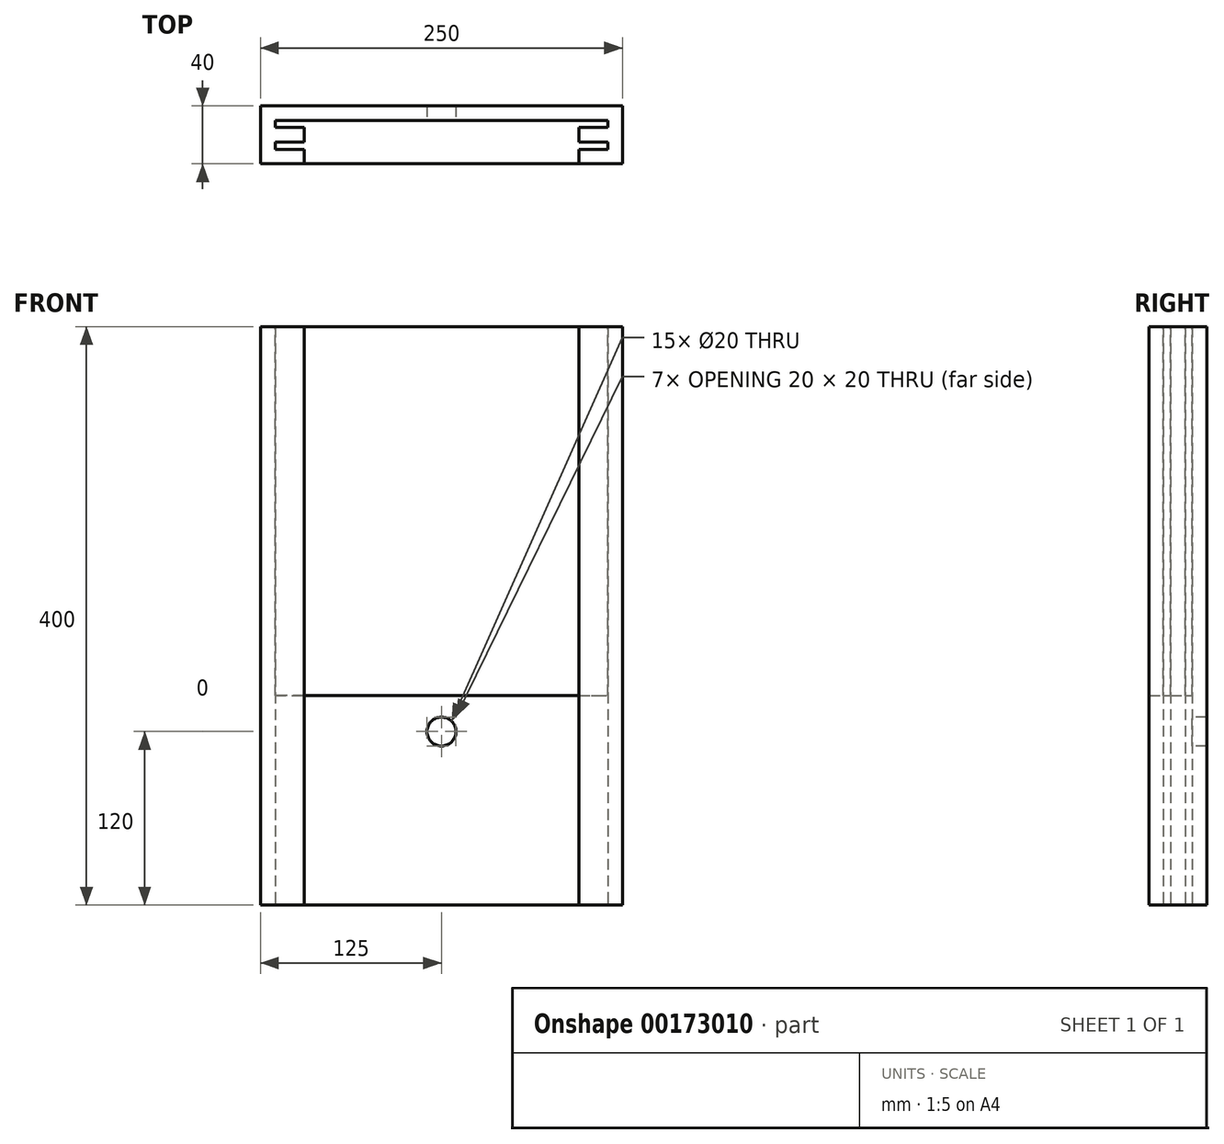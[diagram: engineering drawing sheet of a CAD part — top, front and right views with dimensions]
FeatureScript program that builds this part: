
annotation { "Feature Type Name" : "Feature", "Feature Type Description" : "" }
export const myFeature = defineFeature(function(context is Context, id is Id, definition is map)
    precondition{}
    {
        {
            var Q0;
            Q0=qCreatedBy(makeId("Top.planeOp"),FACE);
            var sketch = newSketch(context, id + "F0", { "sketchPlane" : qUnion([Q0])});
            skLineSegment(sketch, "E0", {"start": v(0, 40) * mm, "end": v(125, 40) * mm});
            skLineSegment(sketch, "E1", {"start": v(125, 40) * mm, "end": v(125, 0) * mm});
            skLineSegment(sketch, "E2", {"start": v(125, 0) * mm, "end": v(95, 0) * mm});
            skLineSegment(sketch, "E3", {"start": v(95, 0) * mm, "end": v(95, 10) * mm});
            skLineSegment(sketch, "E4", {"start": v(95, 10) * mm, "end": v(115, 10) * mm});
            skLineSegment(sketch, "E5", {"start": v(115, 10) * mm, "end": v(115, 15) * mm});
            skLineSegment(sketch, "E6", {"start": v(115, 15) * mm, "end": v(95, 15) * mm});
            skLineSegment(sketch, "E7", {"start": v(95, 15) * mm, "end": v(95, 25) * mm});
            skLineSegment(sketch, "E8", {"start": v(95, 25) * mm, "end": v(115, 25) * mm});
            skLineSegment(sketch, "E9", {"start": v(115, 25) * mm, "end": v(115, 30) * mm});
            skLineSegment(sketch, "E10", {"start": v(115, 30) * mm, "end": v(0, 30) * mm});
            skLineSegment(sketch, "E11", {"start": v(0, 40) * mm, "end": v(0, 0) * mm, "construction": true});
            skLineSegment(sketch, "E12.MirrorCS", {"start": v(0, 40) * mm, "end": v(-125, 40) * mm});
            skLineSegment(sketch, "E13.MirrorCS", {"start": v(-115, 30) * mm, "end": v(0, 30) * mm});
            skLineSegment(sketch, "E14.MirrorCS", {"start": v(-125, 40) * mm, "end": v(-125, 0) * mm});
            skLineSegment(sketch, "E15.MirrorCS", {"start": v(-115, 25) * mm, "end": v(-115, 30) * mm});
            skLineSegment(sketch, "E16.MirrorCS", {"start": v(-95, 25) * mm, "end": v(-115, 25) * mm});
            skLineSegment(sketch, "E17.MirrorCS", {"start": v(-95, 15) * mm, "end": v(-95, 25) * mm});
            skLineSegment(sketch, "E18.MirrorCS", {"start": v(-115, 15) * mm, "end": v(-95, 15) * mm});
            skLineSegment(sketch, "E19.MirrorCS", {"start": v(-115, 10) * mm, "end": v(-115, 15) * mm});
            skLineSegment(sketch, "E20.MirrorCS", {"start": v(-95, 10) * mm, "end": v(-115, 10) * mm});
            skLineSegment(sketch, "E21.MirrorCS", {"start": v(-95, 0) * mm, "end": v(-95, 10) * mm});
            skLineSegment(sketch, "E22.MirrorCS", {"start": v(-125, 0) * mm, "end": v(-95, 0) * mm});
            skSolve(sketch);
        }
        {
            var Q0;
            Q0 = qSketchRegion(id + "F0", true);
            extrude(context, id + "F1", {"entities" : qUnion([Q0]), "depth" : 280 * mm, "hasSecondDirection" : true, "secondDirectionOppositeDirection" : true, "secondDirectionDepth" : 120 * mm});
        }
        {
            var Q0;
            Q0=makeQuery(id+"F1.opExtrude","SWEPT_FACE",FACE,{"disambiguationData":[OSD([sQuery(id+"F0.wireOp",EDGE,"E10"),sQuery(id+"F0.wireOp",EDGE,"E13.MirrorCS")])]});
            var sketch = newSketch(context, id + "F2", { "sketchPlane" : qUnion([Q0])});
            skCircle(sketch, "E23", {"center": v(0, 0) * mm, "radius": 10 * mm});
            skSolve(sketch);
        }
        {
            var Q0;
            Q0 = qSketchRegion(id + "F2", true);
            extrude(context, id + "F3", {"entities" : qUnion([Q0]), "operationType" : NewBodyOperationType.REMOVE, "oppositeDirection" : true, "depth" : 20 * mm});
        }
        {
            var Q0;
            Q0=makeQuery(id+"F1.opExtrude","CAP_FACE",FACE,{"disambiguationData":[OSD([sQuery(id+"F0.wireOp",EDGE,"E0"),sQuery(id+"F0.wireOp",EDGE,"E1"),sQuery(id+"F0.wireOp",EDGE,"E2"),sQuery(id+"F0.wireOp",EDGE,"E3"),sQuery(id+"F0.wireOp",EDGE,"E4"),sQuery(id+"F0.wireOp",EDGE,"E5"),sQuery(id+"F0.wireOp",EDGE,"E6"),sQuery(id+"F0.wireOp",EDGE,"E7"),sQuery(id+"F0.wireOp",EDGE,"E8"),sQuery(id+"F0.wireOp",EDGE,"E9"),sQuery(id+"F0.wireOp",EDGE,"E10"),sQuery(id+"F0.wireOp",EDGE,"E12.MirrorCS"),sQuery(id+"F0.wireOp",EDGE,"E13.MirrorCS"),sQuery(id+"F0.wireOp",EDGE,"E14.MirrorCS"),sQuery(id+"F0.wireOp",EDGE,"E15.MirrorCS"),sQuery(id+"F0.wireOp",EDGE,"E16.MirrorCS"),sQuery(id+"F0.wireOp",EDGE,"E17.MirrorCS"),sQuery(id+"F0.wireOp",EDGE,"E18.MirrorCS"),sQuery(id+"F0.wireOp",EDGE,"E19.MirrorCS"),sQuery(id+"F0.wireOp",EDGE,"E20.MirrorCS"),sQuery(id+"F0.wireOp",EDGE,"E21.MirrorCS"),sQuery(id+"F0.wireOp",EDGE,"E22.MirrorCS")])],"isStart":false});
            var sketch = newSketch(context, id + "F4", { "sketchPlane" : qUnion([Q0])});
            skLineSegment(sketch, "E24", {"start": v(-115, 30) * mm, "end": v(-115, 25) * mm});
            skLineSegment(sketch, "E25", {"start": v(-115, 25) * mm, "end": v(-95, 25) * mm});
            skLineSegment(sketch, "E26", {"start": v(-95, 25) * mm, "end": v(-95, 15) * mm});
            skLineSegment(sketch, "E27", {"start": v(-95, 15) * mm, "end": v(-115, 15) * mm});
            skLineSegment(sketch, "E28", {"start": v(-115, 15) * mm, "end": v(-115, 10) * mm});
            skLineSegment(sketch, "E29", {"start": v(-115, 10) * mm, "end": v(-95, 10) * mm});
            skLineSegment(sketch, "E30", {"start": v(-95, 10) * mm, "end": v(-95, 0) * mm});
            skLineSegment(sketch, "E31", {"start": v(-95, 0) * mm, "end": v(95, 0) * mm});
            skLineSegment(sketch, "E32", {"start": v(95, 0) * mm, "end": v(95, 10) * mm});
            skLineSegment(sketch, "E33", {"start": v(95, 10) * mm, "end": v(115, 10) * mm});
            skLineSegment(sketch, "E34", {"start": v(115, 10) * mm, "end": v(115, 15) * mm});
            skLineSegment(sketch, "E35", {"start": v(115, 15) * mm, "end": v(95, 15) * mm});
            skLineSegment(sketch, "E36", {"start": v(95, 15) * mm, "end": v(95, 25) * mm});
            skLineSegment(sketch, "E37", {"start": v(95, 25) * mm, "end": v(115, 25) * mm});
            skLineSegment(sketch, "E38", {"start": v(115, 25) * mm, "end": v(115, 30) * mm});
            skLineSegment(sketch, "E39", {"start": v(115, 30) * mm, "end": v(-115, 30) * mm});
            skSolve(sketch);
        }
        {
            var Q0;
            Q0 = qSketchRegion(id + "F4", true);
            extrude(context, id + "F5", {"entities" : qUnion([Q0]), "oppositeDirection" : true, "depth" : 255 * mm});
        }
    });
